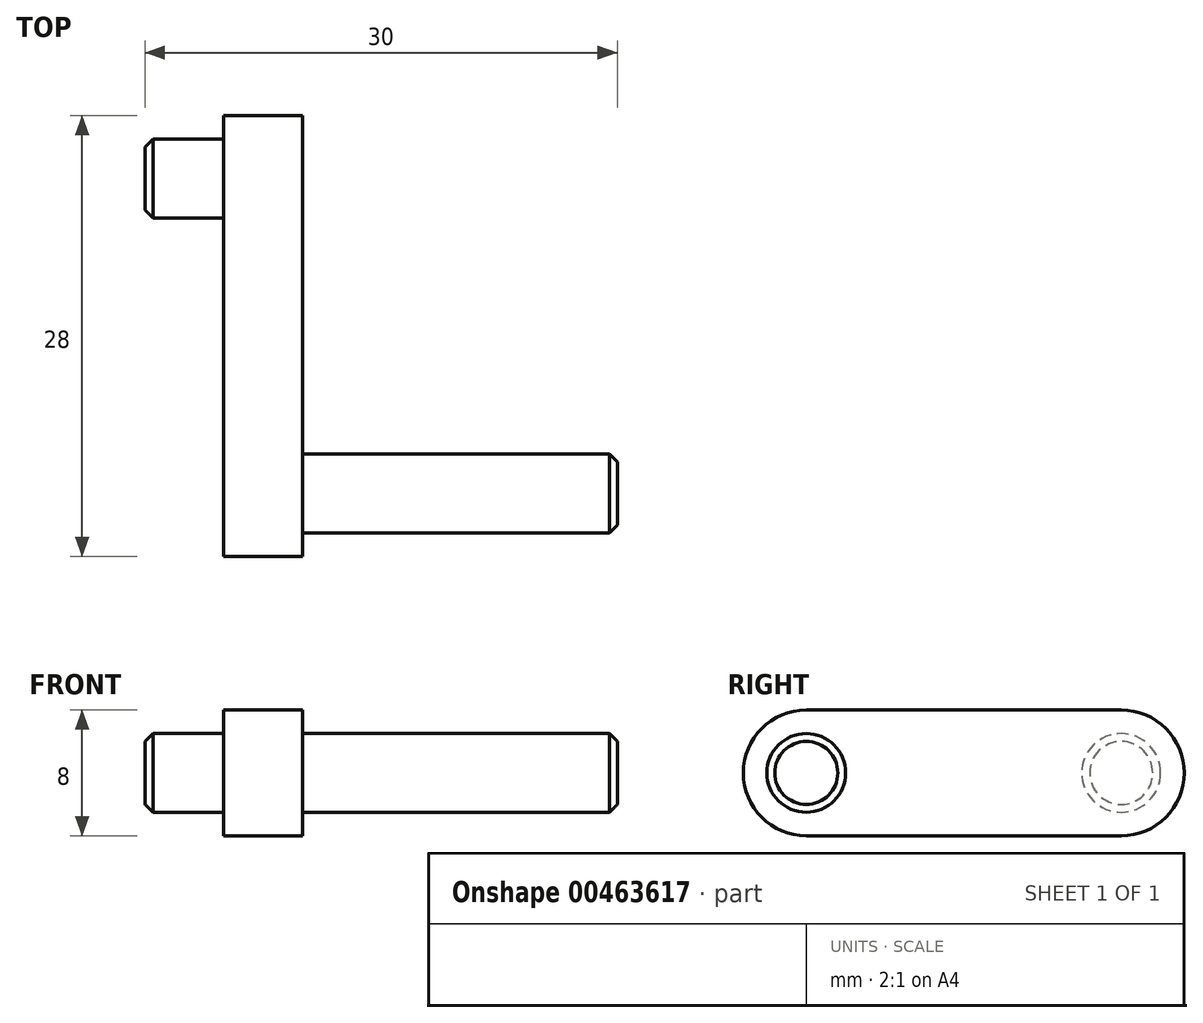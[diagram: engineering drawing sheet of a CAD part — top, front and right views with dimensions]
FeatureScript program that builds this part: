
annotation { "Feature Type Name" : "Feature", "Feature Type Description" : "" }
export const myFeature = defineFeature(function(context is Context, id is Id, definition is map)
    precondition{}
    {
        {
            var Q0;
            Q0=qCreatedBy(makeId("Right.planeOp"),FACE);
            var sketch = newSketch(context, id + "F0", { "sketchPlane" : qUnion([Q0])});
            skCircle(sketch, "E0", {"center": v(4, 0) * mm, "radius": 2.5 * mm});
            skCircle(sketch, "E1", {"center": v(24, 0) * mm, "radius": 2.5 * mm});
            skLineSegment(sketch, "E2.bottom", {"start": v(4, -4) * mm, "end": v(24, -4) * mm});
            skLineSegment(sketch, "E2.top", {"start": v(4, 4) * mm, "end": v(24, 4) * mm});
            skLineSegment(sketch, "E2.left", {"start": v(0, 0) * mm, "end": v(0, 0) * mm});
            skLineSegment(sketch, "E2.right", {"start": v(28, 0) * mm, "end": v(28, 0) * mm});
            skPoint(sketch, "E3.visualSharp", {"position": v(0, 4) * mm});
            skArc(sketch, "E3.filletArc", {"start": v(4, 4) * mm, "mid": v(1.17, 2.83) * mm, "end": v(0, 0) * mm});
            skPoint(sketch, "E4.visualSharp", {"position": v(0, -4) * mm});
            skArc(sketch, "E4.filletArc", {"start": v(0, 0) * mm, "mid": v(1.17, -2.83) * mm, "end": v(4, -4) * mm});
            skPoint(sketch, "E5.visualSharp", {"position": v(28, 4) * mm});
            skArc(sketch, "E5.filletArc", {"start": v(28, 0) * mm, "mid": v(26.83, 2.83) * mm, "end": v(24, 4) * mm});
            skPoint(sketch, "E6.visualSharp", {"position": v(28, -4) * mm});
            skArc(sketch, "E6.filletArc", {"start": v(24, -4) * mm, "mid": v(26.83, -2.83) * mm, "end": v(28, 0) * mm});
            skSolve(sketch);
        }
        {
            var Q0;
            Q0=makeQuery(id+"F0.imprint","IMPRINT",FACE,{"disambiguationData":[TD([[makeQuery(id+"F0.imprint","IMPRINT",EDGE,{"derivedFrom":sQuery(id+"F0.wireOp",EDGE,"E0")}),1.0]])]});
            extrude(context, id + "F1", {"entities" : qUnion([Q0]), "depth" : 25 * mm});
        }
        {
            var Q0;
            Q0=makeQuery(id+"F0.imprint","IMPRINT",FACE,{"disambiguationData":[TD([[makeQuery(id+"F0.imprint","IMPRINT",EDGE,{"derivedFrom":sQuery(id+"F0.wireOp",EDGE,"E0")}),-1.0]])]});
            extrude(context, id + "F2", {"entities" : qUnion([Q0]), "operationType" : NewBodyOperationType.ADD, "depth" : 5 * mm});
        }
        {
            var Q0;
            Q0=makeQuery(id+"F0.imprint","IMPRINT",FACE,{"disambiguationData":[TD([[makeQuery(id+"F0.imprint","IMPRINT",EDGE,{"derivedFrom":sQuery(id+"F0.wireOp",EDGE,"E1")}),1.0]])]});
            extrude(context, id + "F3", {"entities" : qUnion([Q0]), "operationType" : NewBodyOperationType.ADD, "oppositeDirection" : true, "depth" : 5 * mm, "hasSecondDirection" : true, "secondDirectionOppositeDirection" : false, "secondDirectionDepth" : 5 * mm});
        }
        {
            var Q0;
            Q0=makeQuery(id+"F3.opExtrude","CAP_EDGE",EDGE,{"disambiguationData":[OSD([sQuery(id+"F0.wireOp",EDGE,"E1")])],"isStart":false});
            var Q1;
            Q1=makeQuery(id+"F1.opExtrude","CAP_EDGE",EDGE,{"disambiguationData":[OSD([sQuery(id+"F0.wireOp",EDGE,"E0")])],"isStart":false});
            chamfer(context, id + "F4", {"entities" : qUnion([Q0, Q1]), "width" : 0.5 * mm, "tangentPropagation" : true});
        }
    });
